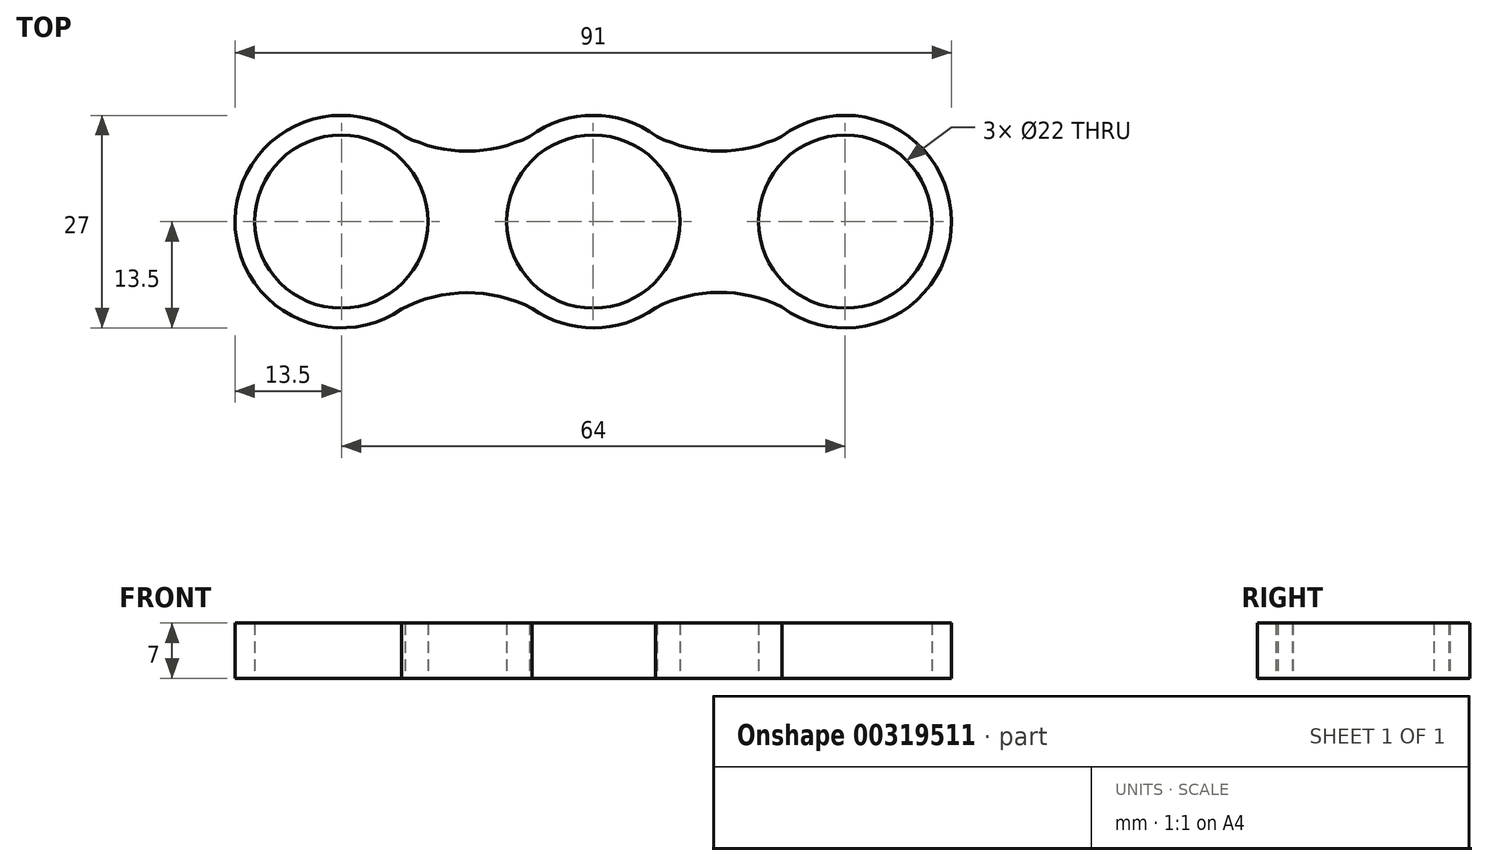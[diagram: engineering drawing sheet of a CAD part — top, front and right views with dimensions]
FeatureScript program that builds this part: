
annotation { "Feature Type Name" : "Feature", "Feature Type Description" : "" }
export const myFeature = defineFeature(function(context is Context, id is Id, definition is map)
    precondition{}
    {
        {
            var Q0;
            Q0=qCreatedBy(makeId("Top.planeOp"),FACE);
            var sketch = newSketch(context, id + "F0", { "sketchPlane" : qUnion([Q0])});
            skCircle(sketch, "E0", {"center": v(-32, 0) * mm, "radius": 11 * mm});
            skCircle(sketch, "E1", {"center": v(-32, 0) * mm, "radius": 13.5 * mm});
            skCircle(sketch, "E2", {"center": v(0, 0) * mm, "radius": 13.5 * mm});
            skCircle(sketch, "E3", {"center": v(0, 0) * mm, "radius": 11 * mm});
            skCircle(sketch, "E4", {"center": v(32, 0) * mm, "radius": 13.5 * mm});
            skCircle(sketch, "E5", {"center": v(32, 0) * mm, "radius": 11 * mm});
            skLineSegment(sketch, "E6", {"start": v(-80.61, -11.44) * mm, "end": v(72.55, -10.6) * mm, "construction": true});
            skLineSegment(sketch, "E7", {"start": v(-81.4, 10.83) * mm, "end": v(77.3, 10.83) * mm, "construction": true});
            skArc(sketch, "E8", {"start": v(-23.94, 10.83) * mm, "mid": v(-16, 8.96) * mm, "end": v(-8.06, 10.83) * mm});
            skArc(sketch, "E9", {"start": v(-7.77, -11.04) * mm, "mid": v(-16.08, -9.03) * mm, "end": v(-24.36, -11.13) * mm});
            skArc(sketch, "E10", {"start": v(24, -10.87) * mm, "mid": v(15.93, -8.98) * mm, "end": v(7.89, -10.96) * mm});
            skArc(sketch, "E11", {"start": v(8.06, 10.83) * mm, "mid": v(16, 8.96) * mm, "end": v(23.94, 10.83) * mm});
            skLineSegment(sketch, "E12", {"start": v(-32, 29.79) * mm, "end": v(-32, -34.2) * mm, "construction": true});
            skLineSegment(sketch, "E13", {"start": v(0, 43.52) * mm, "end": v(0.44, -36.94) * mm, "construction": true});
            skLineSegment(sketch, "E14", {"start": v(32, 40.51) * mm, "end": v(32, -34.49) * mm, "construction": true});
            skSolve(sketch);
        }
        {
            var Q0;
            Q0 = qSketchRegion(id + "F0", true);
            extrude(context, id + "F1", {"entities" : qUnion([Q0]), "depth" : 7 * mm});
        }
    });
